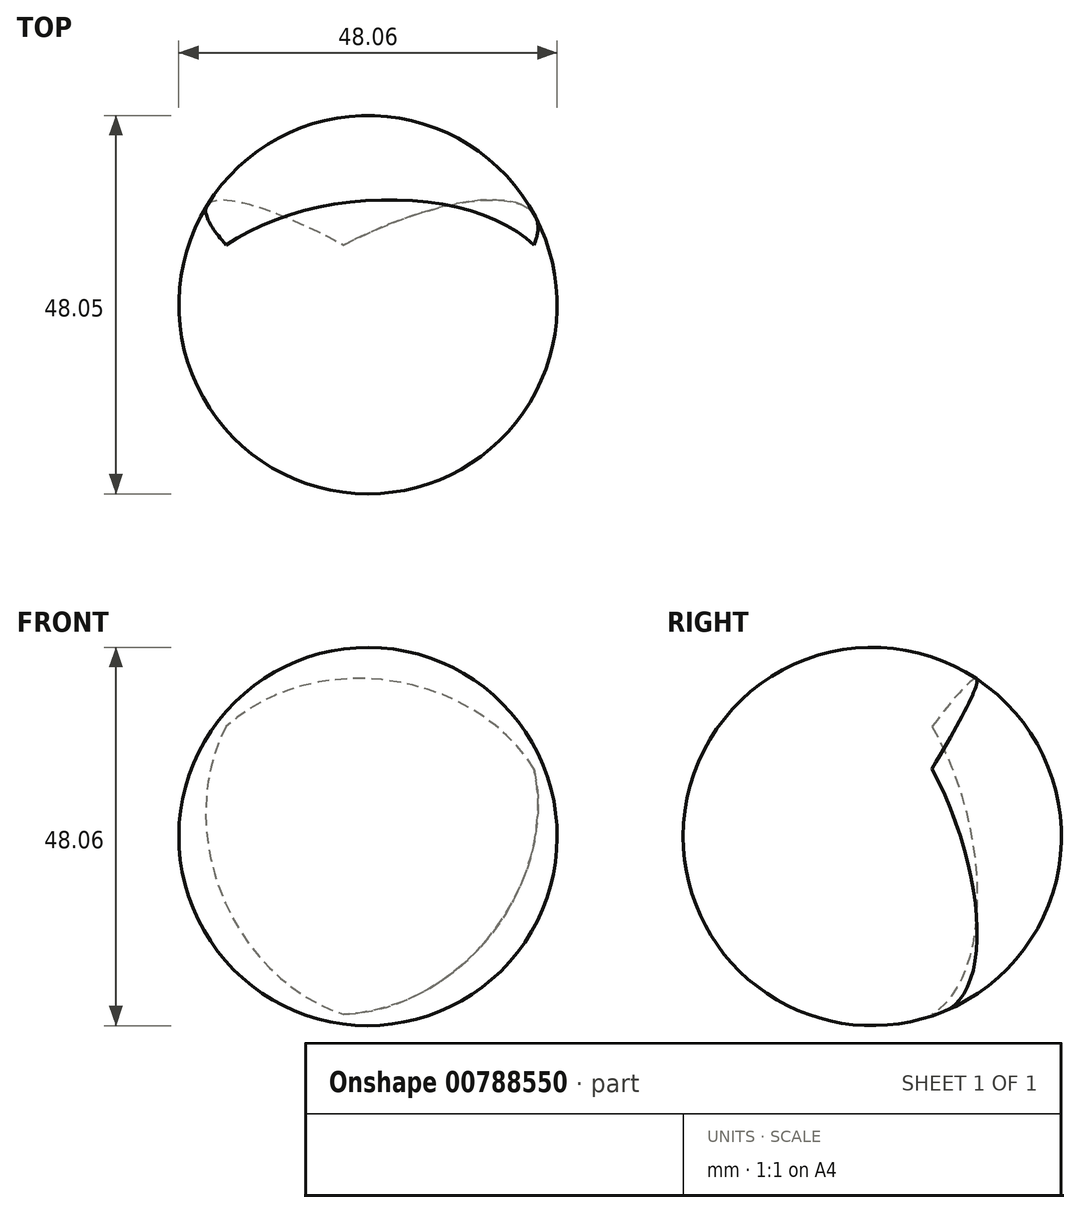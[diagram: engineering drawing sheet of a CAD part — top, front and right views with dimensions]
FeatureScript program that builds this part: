
annotation { "Feature Type Name" : "Feature", "Feature Type Description" : "" }
export const myFeature = defineFeature(function(context is Context, id is Id, definition is map)
    precondition{}
    {
        {
            var Q0;
            Q0=qCreatedBy(makeId("Front.planeOp"),FACE);
            var sketch = newSketch(context, id + "F0", { "sketchPlane" : qUnion([Q0])});
            skCircle(sketch, "E0.cCircle", {"center": v(0, 0) * mm, "radius": 33.33 * mm, "construction": true});
            skLineSegment(sketch, "E0.0", {"start": v(-61.72, -25.2) * mm, "end": v(9.04, 66.05) * mm});
            skLineSegment(sketch, "E0.1", {"start": v(9.04, 66.05) * mm, "end": v(52.68, -40.86) * mm});
            skLineSegment(sketch, "E0.2", {"start": v(52.68, -40.86) * mm, "end": v(-61.72, -25.2) * mm});
            skPoint(sketch, "E0.0.midPoint", {"position": v(-26.34, 20.43) * mm});
            skPoint(sketch, "E1", {"position": v(-4.52, -33.03) * mm});
            skSolve(sketch);
        }
        {
            var Q0;
            Q0=qCreatedBy(makeId("Top.planeOp"),FACE);
            var sketch = newSketch(context, id + "F1", { "sketchPlane" : qUnion([Q0])});
            skLineSegment(sketch, "E2", {"start": v(0, 0) * mm, "end": v(0, 100) * mm});
            skSolve(sketch);
        }
        {
            var Q0;
            Q0=makeQuery(id+"F0.imprint","IMPRINT",FACE,{"disambiguationData":[TD([[makeQuery(id+"F0.imprint","IMPRINT",EDGE,{"derivedFrom":sQuery(id+"F0.wireOp",EDGE,"E0.0")}),-1.0]])]});
            var Q1;
            Q1=sQuery(id+"F1.wireOp",VERTEX,"E2.end");
            loft(context, id + "F2", {"sheetProfilesArray" : [{ "sheetProfileEntities" : qUnion([Q0]) }, { "sheetProfileEntities" : qUnion([Q1]) }]});
        }
        {
            var Q0;
            Q0=makeQuery(id+"F2.opLoft","SWEPT_EDGE",EDGE,{"disambiguationData":[OSD([sQuery(id+"F0.wireOp",EDGE,"E0.0"),sQuery(id+"F0.wireOp",EDGE,"E0.2"),sQuery(id+"F1.wireOp",VERTEX,"E2.end")])]});
            var Q1;
            Q1=makeQuery(id+"F2.opLoft","SWEPT_EDGE",EDGE,{"disambiguationData":[OSD([sQuery(id+"F0.wireOp",EDGE,"E0.0"),sQuery(id+"F0.wireOp",EDGE,"E0.1"),sQuery(id+"F1.wireOp",VERTEX,"E2.end")])]});
            var Q2;
            {var subQ0=sQuery(id+"F0.wireOp",EDGE,"E0.0");var subQ1=sQuery(id+"F0.wireOp",EDGE,"E0.1");var subQ2=sQuery(id+"F0.wireOp",EDGE,"E0.2");Q2=makeQuery(id+"F2.opLoft","MID_CAP_EDGE",EDGE,{"disambiguationData":[OSD([subQ0,subQ1,subQ2]),TDD([makeQuery(id+"F0.imprint","INTERSECT",VERTEX,{"derivedFrom":[subQ0,subQ2]}),makeQuery(id+"F0.imprint","INTERSECT",VERTEX,{"derivedFrom":[subQ0,subQ1]}),makeQuery(id+"F0.imprint","IMPRINT",EDGE,{"derivedFrom":subQ0})])],"capPos":0.0});}
            var Q3;
            {var subQ0=sQuery(id+"F0.wireOp",EDGE,"E0.2");var subQ1=sQuery(id+"F0.wireOp",EDGE,"E0.1");var subQ2=sQuery(id+"F0.wireOp",EDGE,"E0.0");Q3=makeQuery(id+"F2.opLoft","MID_CAP_EDGE",EDGE,{"disambiguationData":[OSD([subQ2,subQ1,subQ0]),TDD([makeQuery(id+"F0.imprint","INTERSECT",VERTEX,{"derivedFrom":[subQ2,subQ0]}),makeQuery(id+"F0.imprint","INTERSECT",VERTEX,{"derivedFrom":[subQ1,subQ0]}),makeQuery(id+"F0.imprint","IMPRINT",EDGE,{"derivedFrom":subQ0})])],"capPos":0.0});}
            var Q4;
            {var subQ0=sQuery(id+"F0.wireOp",EDGE,"E0.1");var subQ1=sQuery(id+"F0.wireOp",EDGE,"E0.2");var subQ2=sQuery(id+"F0.wireOp",EDGE,"E0.0");Q4=makeQuery(id+"F2.opLoft","MID_CAP_EDGE",EDGE,{"disambiguationData":[OSD([subQ2,subQ0,subQ1]),TDD([makeQuery(id+"F0.imprint","INTERSECT",VERTEX,{"derivedFrom":[subQ2,subQ0]}),makeQuery(id+"F0.imprint","INTERSECT",VERTEX,{"derivedFrom":[subQ0,subQ1]}),makeQuery(id+"F0.imprint","IMPRINT",EDGE,{"derivedFrom":subQ0})])],"capPos":0.0});}
            var Q5;
            Q5=makeQuery(id+"F2.opLoft","SWEPT_EDGE",EDGE,{"disambiguationData":[OSD([sQuery(id+"F0.wireOp",EDGE,"E0.1"),sQuery(id+"F0.wireOp",EDGE,"E0.2"),sQuery(id+"F1.wireOp",VERTEX,"E2.end")])]});
            fillet(context, id + "F3", {"entities" : qUnion([Q0, Q1, Q2, Q3, Q4, Q5]), "radius" : 24.03 * mm, "tangentPropagation" : true, "allowEdgeOverflow" : false});
        }
    });
